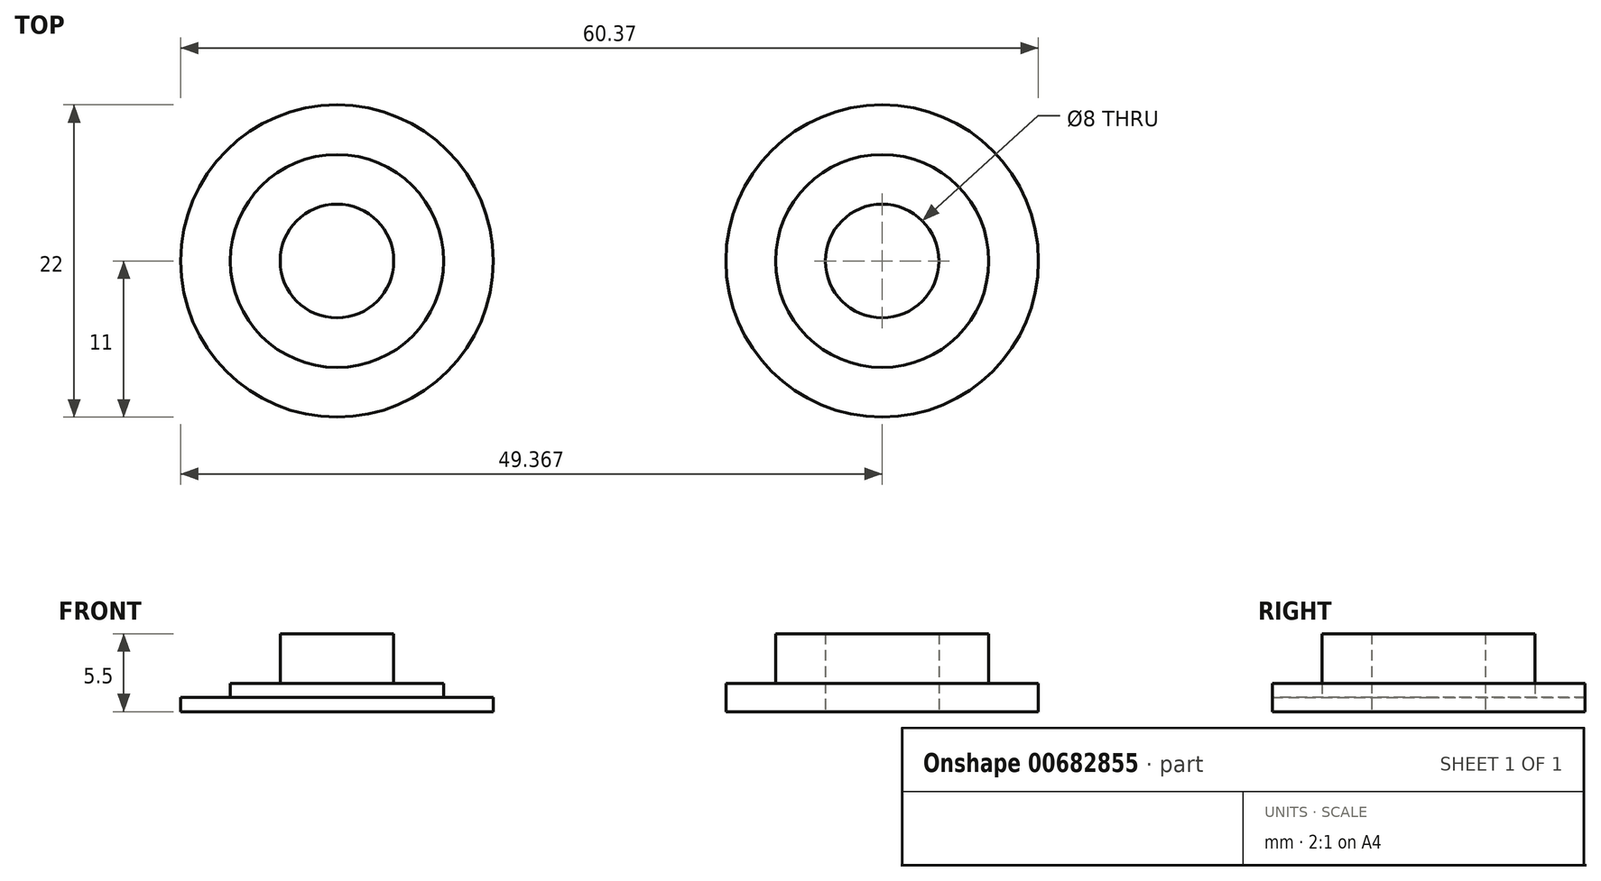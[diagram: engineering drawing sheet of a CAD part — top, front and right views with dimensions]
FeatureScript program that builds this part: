
annotation { "Feature Type Name" : "Feature", "Feature Type Description" : "" }
export const myFeature = defineFeature(function(context is Context, id is Id, definition is map)
    precondition{}
    {
        {
            var Q0;
            Q0=qCreatedBy(makeId("Top.planeOp"),FACE);
            var sketch = newSketch(context, id + "F0", { "sketchPlane" : qUnion([Q0])});
            skCircle(sketch, "E0", {"center": v(0, 0) * mm, "radius": 11 * mm});
            skCircle(sketch, "E1", {"center": v(0, 0) * mm, "radius": 7.5 * mm});
            skCircle(sketch, "E2", {"center": v(0, 0) * mm, "radius": 4 * mm});
            skCircle(sketch, "E3.MirrorC", {"center": v(38.37, 0) * mm, "radius": 11 * mm});
            skCircle(sketch, "E4.MirrorC", {"center": v(38.37, 0) * mm, "radius": 7.5 * mm});
            skCircle(sketch, "E5.MirrorC", {"center": v(38.37, 0) * mm, "radius": 4 * mm});
            skSolve(sketch);
        }
        {
            var Q0;
            Q0=makeQuery(id+"F0.imprint","IMPRINT",FACE,{"disambiguationData":[TD([[makeQuery(id+"F0.imprint","IMPRINT",EDGE,{"derivedFrom":sQuery(id+"F0.wireOp",EDGE,"E0")}),1.0]])]});
            var Q1;
            Q1=makeQuery(id+"F0.imprint","IMPRINT",FACE,{"disambiguationData":[TD([[makeQuery(id+"F0.imprint","IMPRINT",EDGE,{"derivedFrom":sQuery(id+"F0.wireOp",EDGE,"E3.MirrorC")}),-1.0]])]});
            extrude(context, id + "F1", {"entities" : qUnion([Q0, Q1]), "depth" : 1 * mm, "offsetDistance" : 25 * mm});
        }
        {
            var Q0;
            Q0=makeQuery(id+"F0.imprint","IMPRINT",FACE,{"disambiguationData":[TD([[makeQuery(id+"F0.imprint","IMPRINT",EDGE,{"derivedFrom":sQuery(id+"F0.wireOp",EDGE,"E1")}),1.0]])]});
            var Q1;
            Q1=makeQuery(id+"F0.imprint","IMPRINT",FACE,{"disambiguationData":[TD([[makeQuery(id+"F0.imprint","IMPRINT",EDGE,{"derivedFrom":sQuery(id+"F0.wireOp",EDGE,"E4.MirrorC")}),-1.0]])]});
            extrude(context, id + "F2", {"entities" : qUnion([Q0, Q1]), "operationType" : NewBodyOperationType.ADD, "depth" : 2 * mm, "offsetDistance" : 25 * mm});
        }
        {
            var Q0;
            Q0=makeQuery(id+"F0.imprint","IMPRINT",FACE,{"disambiguationData":[TD([[makeQuery(id+"F0.imprint","IMPRINT",EDGE,{"derivedFrom":sQuery(id+"F0.wireOp",EDGE,"E2")}),1.0]])]});
            var Q1;
            Q1=makeQuery(id+"F0.imprint","IMPRINT",FACE,{"disambiguationData":[TD([[makeQuery(id+"F0.imprint","IMPRINT",EDGE,{"derivedFrom":sQuery(id+"F0.wireOp",EDGE,"E5.MirrorC")}),-1.0]])]});
            extrude(context, id + "F3", {"entities" : qUnion([Q0, Q1]), "operationType" : NewBodyOperationType.ADD, "depth" : 5.5 * mm, "offsetDistance" : 25 * mm});
        }
    });
